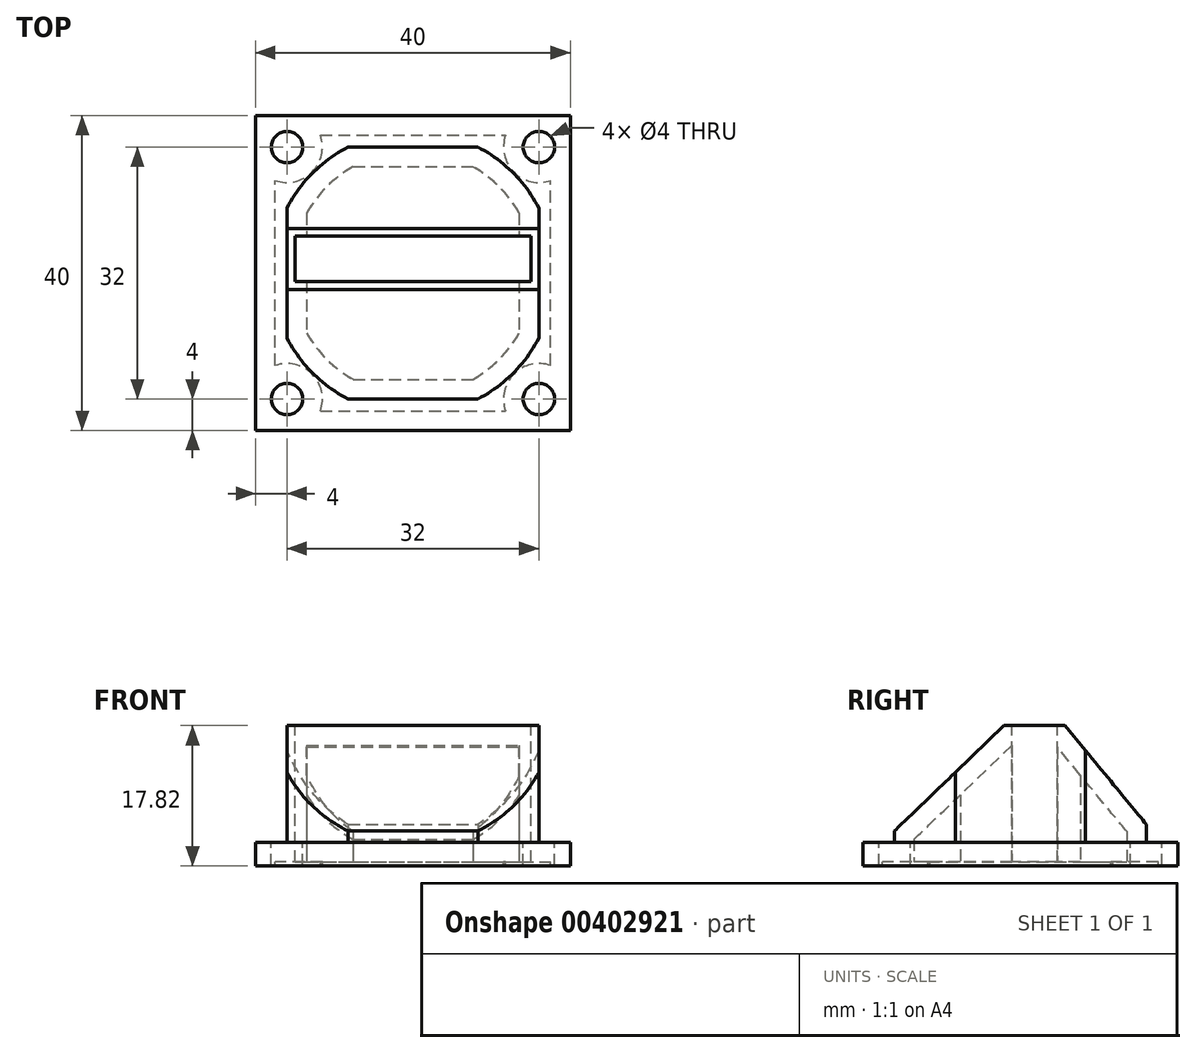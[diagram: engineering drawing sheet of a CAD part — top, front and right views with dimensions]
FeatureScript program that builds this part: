
annotation { "Feature Type Name" : "Feature", "Feature Type Description" : "" }
export const myFeature = defineFeature(function(context is Context, id is Id, definition is map)
    precondition{}
    {
        {
            var Q0;
            Q0=qCreatedBy(makeId("Top.planeOp"),FACE);
            var sketch = newSketch(context, id + "F0", { "sketchPlane" : qUnion([Q0])});
            skLineSegment(sketch, "E0.bottom", {"start": v(0, 0) * mm, "end": v(40, 0) * mm});
            skLineSegment(sketch, "E0.top", {"start": v(0, 40) * mm, "end": v(40, 40) * mm});
            skLineSegment(sketch, "E0.left", {"start": v(0, 0) * mm, "end": v(0, 40) * mm});
            skLineSegment(sketch, "E0.right", {"start": v(40, 0) * mm, "end": v(40, 40) * mm});
            skSolve(sketch);
        }
        {
            var Q0;
            Q0 = qSketchRegion(id + "F0", true);
            extrude(context, id + "F1", {"entities" : qUnion([Q0]), "depth" : 3 * mm, "offsetDistance" : 25 * mm});
        }
        {
            var Q0;
            Q0=makeQuery(id+"F1.opExtrude","CAP_FACE",FACE,{"disambiguationData":[OSD([sQuery(id+"F0.wireOp",EDGE,"E0.bottom"),sQuery(id+"F0.wireOp",EDGE,"E0.top"),sQuery(id+"F0.wireOp",EDGE,"E0.left"),sQuery(id+"F0.wireOp",EDGE,"E0.right")])],"isStart":false});
            var sketch = newSketch(context, id + "F2", { "sketchPlane" : qUnion([Q0])});
            skCircle(sketch, "E1", {"center": v(4, 36) * mm, "radius": 2 * mm});
            skCircle(sketch, "E2", {"center": v(36, 36) * mm, "radius": 2 * mm});
            skCircle(sketch, "E3", {"center": v(36, 4) * mm, "radius": 2 * mm});
            skCircle(sketch, "E4", {"center": v(4, 4) * mm, "radius": 2 * mm});
            skSolve(sketch);
        }
        {
            var Q0;
            Q0 = qSketchRegion(id + "F2", true);
            extrude(context, id + "F3", {"entities" : qUnion([Q0]), "operationType" : NewBodyOperationType.REMOVE, "oppositeDirection" : true, "depth" : 25 * mm, "offsetDistance" : 25 * mm});
        }
        {
            var Q0;
            Q0=makeQuery(id+"F1.opExtrude","CAP_FACE",FACE,{"disambiguationData":[OSD([sQuery(id+"F0.wireOp",EDGE,"E0.bottom"),sQuery(id+"F0.wireOp",EDGE,"E0.top"),sQuery(id+"F0.wireOp",EDGE,"E0.left"),sQuery(id+"F0.wireOp",EDGE,"E0.right")])],"isStart":false});
            var sketch = newSketch(context, id + "F4", { "sketchPlane" : qUnion([Q0])});
            skLineSegment(sketch, "E5.bottom", {"start": v(11.75, 36) * mm, "end": v(28.25, 36) * mm});
            skLineSegment(sketch, "E5.top", {"start": v(11.75, 4) * mm, "end": v(28.25, 4) * mm});
            skLineSegment(sketch, "E5.left", {"start": v(4, 28.25) * mm, "end": v(4, 11.75) * mm});
            skLineSegment(sketch, "E5.right", {"start": v(36, 28.25) * mm, "end": v(36, 11.75) * mm});
            skArc(sketch, "E6", {"start": v(11.75, 36) * mm, "mid": v(7.27, 32.73) * mm, "end": v(4, 28.25) * mm});
            skPoint(sketch, "E6.centerSnap0", {"position": v(40, 20) * mm});
            skPoint(sketch, "E6.centerSnap1", {"position": v(20, 36) * mm});
            skPoint(sketch, "E7.orphan", {"position": v(4, 36) * mm});
            skPoint(sketch, "E8.orphan", {"position": v(36, 36) * mm});
            skArc(sketch, "E9.trimOffspring", {"start": v(36, 28.25) * mm, "mid": v(32.73, 32.73) * mm, "end": v(28.25, 36) * mm});
            skArc(sketch, "E10.trimOffspring", {"start": v(4, 11.75) * mm, "mid": v(7.27, 7.27) * mm, "end": v(11.75, 4) * mm});
            skArc(sketch, "E11.trimOffspring", {"start": v(28.25, 4) * mm, "mid": v(32.73, 7.27) * mm, "end": v(36, 11.75) * mm});
            skPoint(sketch, "E12.orphan", {"position": v(36, 4) * mm});
            skSolve(sketch);
        }
        {
            var Q0;
            Q0 = qSketchRegion(id + "F4", true);
            extrude(context, id + "F5", {"entities" : qUnion([Q0]), "operationType" : NewBodyOperationType.ADD, "depth" : 30 * mm, "offsetDistance" : 25 * mm});
        }
        {
            var Q0;
            Q0=makeQuery(id+"F5.opExtrude","SWEPT_FACE",FACE,{"disambiguationData":[OSD([sQuery(id+"F4.wireOp",EDGE,"E5.right")])]});
            var sketch = newSketch(context, id + "F6", { "sketchPlane" : qUnion([Q0])});
            skLineSegment(sketch, "E13", {"start": v(39.57, 38.6) * mm, "end": v(2.5, 3) * mm});
            skLineSegment(sketch, "E14", {"start": v(2.5, 3) * mm, "end": v(2.5, 41.88) * mm});
            skLineSegment(sketch, "E15", {"start": v(2.5, 41.88) * mm, "end": v(48.47, 41.88) * mm});
            skLineSegment(sketch, "E16", {"start": v(39.57, 38.6) * mm, "end": v(48.47, 41.88) * mm});
            skSolve(sketch);
        }
        {
            var Q0;
            Q0 = qSketchRegion(id + "F6", true);
            extrude(context, id + "F7", {"entities" : qUnion([Q0]), "operationType" : NewBodyOperationType.REMOVE, "endBound" : BoundingType.THROUGH_ALL, "oppositeDirection" : true, "depth" : 25 * mm, "offsetDistance" : 25 * mm});
        }
        {
            var Q0;
            Q0=makeQuery(id+"F5.opExtrude","SWEPT_FACE",FACE,{"disambiguationData":[OSD([sQuery(id+"F4.wireOp",EDGE,"E5.right")])]});
            var sketch = newSketch(context, id + "F8", { "sketchPlane" : qUnion([Q0])});
            skLineSegment(sketch, "E17", {"start": v(36.8, 4.28) * mm, "end": v(20.72, 23.86) * mm});
            skLineSegment(sketch, "E18", {"start": v(20.72, 23.86) * mm, "end": v(20.72, 38.2) * mm});
            skLineSegment(sketch, "E19", {"start": v(20.72, 38.2) * mm, "end": v(40.81, 38.2) * mm});
            skLineSegment(sketch, "E20", {"start": v(40.81, 38.2) * mm, "end": v(36.8, 4.28) * mm});
            skSolve(sketch);
        }
        {
            var Q0;
            Q0 = qSketchRegion(id + "F8", true);
            extrude(context, id + "F9", {"entities" : qUnion([Q0]), "operationType" : NewBodyOperationType.REMOVE, "endBound" : BoundingType.THROUGH_ALL, "oppositeDirection" : true, "depth" : 25 * mm, "offsetDistance" : 25 * mm});
        }
        {
            var Q0;
            Q0=makeQuery(id+"F5.opExtrude","SWEPT_FACE",FACE,{"disambiguationData":[OSD([sQuery(id+"F4.wireOp",EDGE,"E5.right")])]});
            var sketch = newSketch(context, id + "F10", { "sketchPlane" : qUnion([Q0])});
            skLineSegment(sketch, "E21", {"start": v(36.51, 17.82) * mm, "end": v(13.36, 17.82) * mm});
            skLineSegment(sketch, "E22", {"start": v(13.36, 17.82) * mm, "end": v(13.36, 31.58) * mm});
            skLineSegment(sketch, "E23", {"start": v(13.36, 31.58) * mm, "end": v(38.61, 31.58) * mm});
            skLineSegment(sketch, "E24", {"start": v(38.61, 31.58) * mm, "end": v(36.51, 17.82) * mm});
            skSolve(sketch);
        }
        {
            var Q0;
            Q0 = qSketchRegion(id + "F10", true);
            extrude(context, id + "F11", {"entities" : qUnion([Q0]), "operationType" : NewBodyOperationType.REMOVE, "endBound" : BoundingType.THROUGH_ALL, "oppositeDirection" : true, "depth" : 25 * mm, "offsetDistance" : 25 * mm});
        }
        {
            var Q0;
            Q0=makeQuery(id+"F1.opExtrude","CAP_FACE",FACE,{"disambiguationData":[OSD([sQuery(id+"F0.wireOp",EDGE,"E0.bottom"),sQuery(id+"F0.wireOp",EDGE,"E0.top"),sQuery(id+"F0.wireOp",EDGE,"E0.left"),sQuery(id+"F0.wireOp",EDGE,"E0.right")])],"isStart":true});
            shell(context, id + "F12", {"entities" : qUnion([Q0]), "thickness" : 2.5 * mm});
        }
        {
            var Q0;
            Q0=makeQuery(id+"F11.boolean.opBoolean","COPY",FACE,{"derivedFrom":makeQuery(id+"F11.opExtrude","SWEPT_FACE",FACE,{"disambiguationData":[OSD([sQuery(id+"F10.wireOp",EDGE,"E21")])]})});
            var sketch = newSketch(context, id + "F13", { "sketchPlane" : qUnion([Q0])});
            skLineSegment(sketch, "E25.bottom", {"start": v(5, 24.68) * mm, "end": v(35, 24.68) * mm});
            skLineSegment(sketch, "E25.top", {"start": v(5, 18.93) * mm, "end": v(35, 18.93) * mm});
            skLineSegment(sketch, "E25.left", {"start": v(5, 24.68) * mm, "end": v(5, 18.93) * mm});
            skLineSegment(sketch, "E25.right", {"start": v(35, 24.68) * mm, "end": v(35, 18.93) * mm});
            skSolve(sketch);
        }
        {
            var Q0;
            Q0 = qSketchRegion(id + "F13", true);
            extrude(context, id + "F14", {"entities" : qUnion([Q0]), "operationType" : NewBodyOperationType.REMOVE, "oppositeDirection" : true, "depth" : 25 * mm, "offsetDistance" : 25 * mm});
        }
    });
